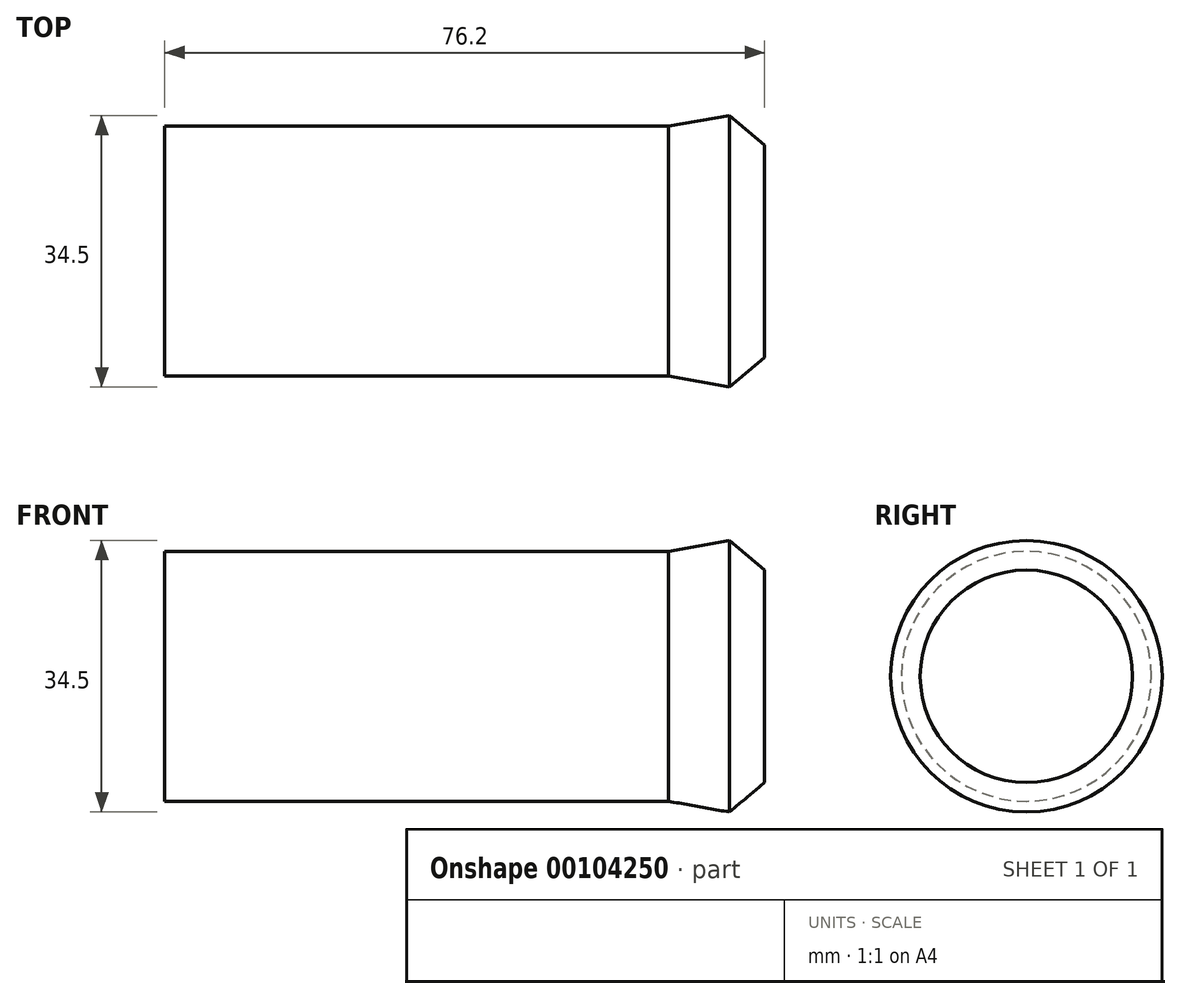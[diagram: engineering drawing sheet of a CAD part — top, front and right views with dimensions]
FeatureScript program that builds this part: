
annotation { "Feature Type Name" : "Feature", "Feature Type Description" : "" }
export const myFeature = defineFeature(function(context is Context, id is Id, definition is map)
    precondition{}
    {
        {
            var Q0;
            Q0=qCreatedBy(makeId("Front.planeOp"),FACE);
            var sketch = newSketch(context, id + "F0", { "sketchPlane" : qUnion([Q0])});
            skLineSegment(sketch, "E0", {"start": v(0, 0) * mm, "end": v(0, 31.75) * mm});
            skLineSegment(sketch, "E1", {"start": v(0, 31.75) * mm, "end": v(-10.16, 31.75) * mm});
            skLineSegment(sketch, "E2", {"start": v(-10.16, 31.75) * mm, "end": v(-10.16, 20.7) * mm});
            skLineSegment(sketch, "E3", {"start": v(0, 0) * mm, "end": v(-76.2, 0) * mm});
            skLineSegment(sketch, "E4", {"start": v(-76.2, 15.88) * mm, "end": v(-12.24, 15.88) * mm});
            skLineSegment(sketch, "E5", {"start": v(-76.2, 0) * mm, "end": v(-76.2, 15.88) * mm});
            skLineSegment(sketch, "E6", {"start": v(0, 0) * mm, "end": v(0, 18.03) * mm});
            skLineSegment(sketch, "E7", {"start": v(-12.24, 15.88) * mm, "end": v(0, 18.03) * mm});
            skPoint(sketch, "E8.orphan", {"position": v(-10.16, 0) * mm});
            skLineSegment(sketch, "E9", {"start": v(-76.2, 18.96) * mm, "end": v(-10.16, 20.7) * mm});
            skLineSegment(sketch, "E10", {"start": v(-76.2, 15.88) * mm, "end": v(-76.2, 18.96) * mm});
            skSolve(sketch);
        }
        {
            var Q0;
            Q0=makeQuery(id+"F0.imprint","IMPRINT",FACE,{"disambiguationData":[TD([[makeQuery(id+"F0.imprint","IMPRINT",EDGE,{"derivedFrom":sQuery(id+"F0.wireOp",EDGE,"E0")}),1.0]])]});
            var Q1;
            Q1=sQuery(id+"F0.wireOp",EDGE,"E3");
            revolve(context, id + "F1", {"entities" : qUnion([Q0]), "axis" : qUnion([Q1]), "revolveType" : RevolveType.FULL});
        }
        {
            var Q0;
            Q0=makeQuery(id+"F1.opRevolve","SWEPT_EDGE",EDGE,{"disambiguationData":[OSD([sQuery(id+"F0.wireOp",EDGE,"E0"),sQuery(id+"F0.wireOp",EDGE,"E1")])]});
            chamfer(context, id + "F2", {"entities" : qUnion([Q0]), "width" : 3.8 * mm, "tangentPropagation" : true});
        }
    });
